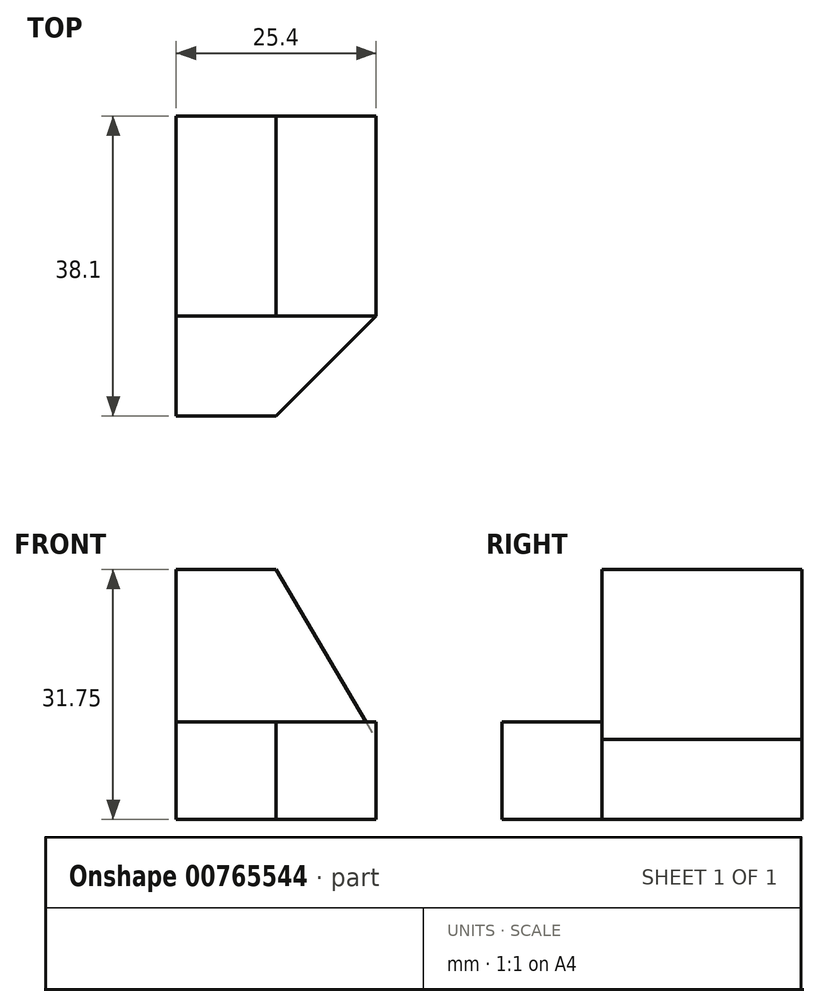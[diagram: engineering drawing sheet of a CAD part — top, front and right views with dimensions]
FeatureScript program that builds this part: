
annotation { "Feature Type Name" : "Feature", "Feature Type Description" : "" }
export const myFeature = defineFeature(function(context is Context, id is Id, definition is map)
    precondition{}
    {
        {
            var Q0;
            Q0=qCreatedBy(makeId("Right.planeOp"),FACE);
            var sketch = newSketch(context, id + "F0", { "sketchPlane" : qUnion([Q0])});
            skLineSegment(sketch, "E0", {"start": v(0, 31.75) * mm, "end": v(0, 0) * mm});
            skLineSegment(sketch, "E1", {"start": v(0, 0) * mm, "end": v(38.1, 0) * mm});
            skLineSegment(sketch, "E2", {"start": v(38.1, 0) * mm, "end": v(38.1, 31.75) * mm});
            skLineSegment(sketch, "E3", {"start": v(38.1, 31.75) * mm, "end": v(0, 31.75) * mm});
            skSolve(sketch);
        }
        {
            var Q0;
            Q0=makeQuery(id+"F0.imprint","IMPRINT",FACE,{"disambiguationData":[TD([[makeQuery(id+"F0.imprint","IMPRINT",EDGE,{"derivedFrom":sQuery(id+"F0.wireOp",EDGE,"E0")}),1.0]])]});
            extrude(context, id + "F1", {"entities" : qUnion([Q0]), "depth" : 25.4 * mm, "offsetDistance" : 25.4 * mm});
        }
        {
            var Q0;
            Q0=makeQuery(id+"F1.opExtrude","CAP_FACE",FACE,{"disambiguationData":[OSD([sQuery(id+"F0.wireOp",EDGE,"E0"),sQuery(id+"F0.wireOp",EDGE,"E1"),sQuery(id+"F0.wireOp",EDGE,"E2"),sQuery(id+"F0.wireOp",EDGE,"E3")])],"isStart":false});
            var sketch = newSketch(context, id + "F2", { "sketchPlane" : qUnion([Q0])});
            skLineSegment(sketch, "E4", {"start": v(0, 31.75) * mm, "end": v(12.7, 31.75) * mm});
            skLineSegment(sketch, "E5", {"start": v(12.7, 31.75) * mm, "end": v(12.7, 12.36) * mm});
            skLineSegment(sketch, "E6", {"start": v(12.7, 12.36) * mm, "end": v(0, 12.36) * mm});
            skLineSegment(sketch, "E7", {"start": v(0, 12.36) * mm, "end": v(0, 31.75) * mm});
            skSolve(sketch);
        }
        {
            var Q0;
            Q0 = qSketchRegion(id + "F2", true);
            extrude(context, id + "F3", {"entities" : qUnion([Q0]), "operationType" : NewBodyOperationType.REMOVE, "oppositeDirection" : true, "depth" : 25.4 * mm, "offsetDistance" : 25.4 * mm});
        }
        {
            var Q0;
            Q0=makeQuery(id+"F1.opExtrude","SWEPT_FACE",FACE,{"disambiguationData":[OSD([sQuery(id+"F0.wireOp",EDGE,"E2")])]});
            var sketch = newSketch(context, id + "F4", { "sketchPlane" : qUnion([Q0])});
            skLineSegment(sketch, "E8", {"start": v(-12.7, 31.75) * mm, "end": v(-25.4, 10.15) * mm});
            skLineSegment(sketch, "E9", {"start": v(-25.4, 10.15) * mm, "end": v(-25.4, 31.75) * mm});
            skLineSegment(sketch, "E10", {"start": v(-25.4, 31.75) * mm, "end": v(-12.7, 31.75) * mm});
            skSolve(sketch);
        }
        {
            var Q0;
            Q0 = qSketchRegion(id + "F4", true);
            extrude(context, id + "F5", {"entities" : qUnion([Q0]), "operationType" : NewBodyOperationType.REMOVE, "oppositeDirection" : true, "depth" : 25.4 * mm, "offsetDistance" : 25.4 * mm});
        }
        {
            var Q0;
            Q0=makeQuery(id+"F3.boolean.opBoolean","COPY",FACE,{"derivedFrom":makeQuery(id+"F3.opExtrude","SWEPT_FACE",FACE,{"disambiguationData":[OSD([sQuery(id+"F2.wireOp",EDGE,"E6")])]})});
            var sketch = newSketch(context, id + "F6", { "sketchPlane" : qUnion([Q0])});
            skLineSegment(sketch, "E11", {"start": v(25.4, 12.7) * mm, "end": v(12.7, 0) * mm});
            skLineSegment(sketch, "E12", {"start": v(12.7, 0) * mm, "end": v(25.4, -12.7) * mm});
            skLineSegment(sketch, "E13", {"start": v(25.4, 12.7) * mm, "end": v(38.1, 0) * mm});
            skSolve(sketch);
        }
        {
            var Q0;
            Q0 = qSketchRegion(id + "F6", true);
            var Q1;
            {var subQ0=sQuery(id+"F6.wireOp",EDGE,"E11");Q1=makeQuery(id+"F6.imprint","IMPRINT",FACE,{"disambiguationData":[TD([[makeQuery(id+"F6.imprint","IMPRINT",EDGE,{"derivedFrom":subQ0}),1.0]])]});}
            extrude(context, id + "F7", {"entities" : qUnion([Q0, Q1]), "operationType" : NewBodyOperationType.REMOVE, "oppositeDirection" : true, "depth" : 25.4 * mm, "offsetDistance" : 25.4 * mm});
        }
    });
